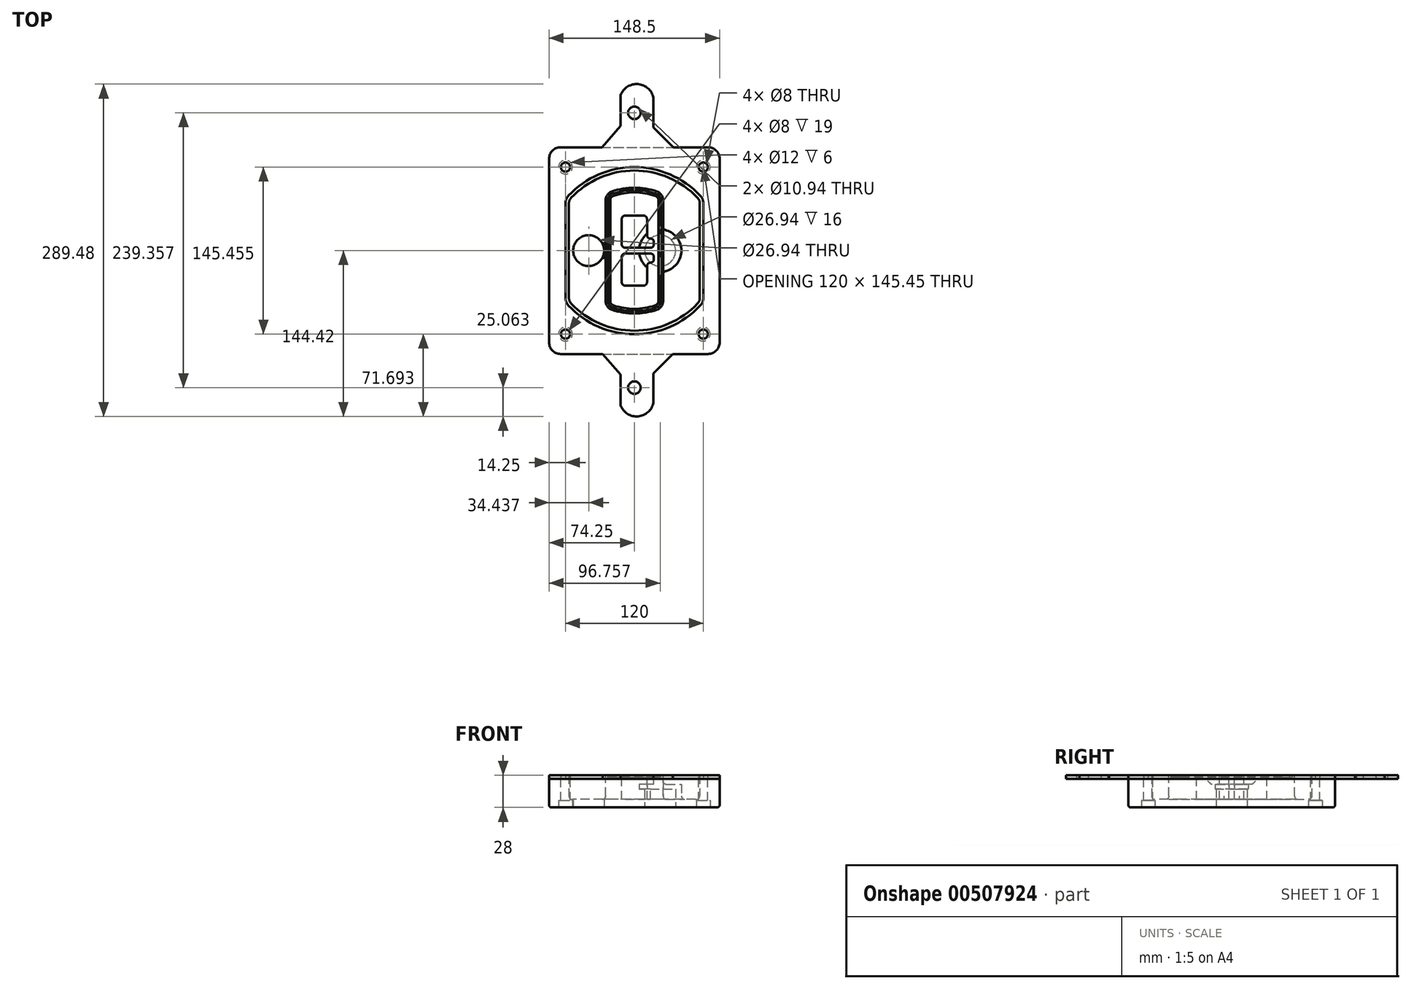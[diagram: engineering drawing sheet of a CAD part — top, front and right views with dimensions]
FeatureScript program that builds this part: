
annotation { "Feature Type Name" : "Feature", "Feature Type Description" : "" }
export const myFeature = defineFeature(function(context is Context, id is Id, definition is map)
    precondition{}
    {
        {
            var Q0;
            Q0=qCreatedBy(makeId("Top.planeOp"),FACE);
            var sketch = newSketch(context, id + "F0", { "sketchPlane" : qUnion([Q0])});
            skPoint(sketch, "E0.rect.middle", {"position": v(0, 0) * mm});
            skLineSegment(sketch, "E1.bottom", {"start": v(-64.25, -90) * mm, "end": v(64.25, -90) * mm});
            skLineSegment(sketch, "E1.top", {"start": v(-64.25, 90) * mm, "end": v(64.25, 90) * mm});
            skLineSegment(sketch, "E1.left", {"start": v(-74.25, -80) * mm, "end": v(-74.25, 80) * mm});
            skLineSegment(sketch, "E1.right", {"start": v(74.25, -80) * mm, "end": v(74.25, 80) * mm});
            skLineSegment(sketch, "E2", {"start": v(-74.25, 90) * mm, "end": v(74.25, -90) * mm, "construction": true});
            skLineSegment(sketch, "E3", {"start": v(74.25, 90) * mm, "end": v(-74.25, -90) * mm, "construction": true});
            skCircle(sketch, "E4", {"center": v(-60, 72.73) * mm, "radius": 4 * mm});
            skCircle(sketch, "E5", {"center": v(60, 72.73) * mm, "radius": 4 * mm});
            skCircle(sketch, "E6", {"center": v(60, -72.73) * mm, "radius": 4 * mm});
            skCircle(sketch, "E7", {"center": v(-60, -72.73) * mm, "radius": 4 * mm});
            skLineSegment(sketch, "E8", {"start": v(-60, 72.73) * mm, "end": v(60, 72.73) * mm, "construction": true});
            skLineSegment(sketch, "E9", {"start": v(60, 72.73) * mm, "end": v(60, -72.73) * mm, "construction": true});
            skLineSegment(sketch, "E10", {"start": v(60, -72.73) * mm, "end": v(-60, -72.73) * mm, "construction": true});
            skLineSegment(sketch, "E11", {"start": v(-60, -72.73) * mm, "end": v(-60, 72.73) * mm, "construction": true});
            skLineSegment(sketch, "E12", {"start": v(-60, 41.18) * mm, "end": v(-60, -41.18) * mm});
            skLineSegment(sketch, "E13", {"start": v(60, 41.18) * mm, "end": v(60, -41.18) * mm});
            skArc(sketch, "E14", {"start": v(57.27, 48.05) * mm, "mid": v(0, 72.73) * mm, "end": v(-57.27, 48.05) * mm});
            skArc(sketch, "E15", {"start": v(-57.27, -48.05) * mm, "mid": v(0, -72.73) * mm, "end": v(57.27, -48.05) * mm});
            skLineSegment(sketch, "E16", {"start": v(-60, 0) * mm, "end": v(60, 0) * mm, "construction": true});
            skPoint(sketch, "E17.visualSharp", {"position": v(-60, -45) * mm});
            skArc(sketch, "E17.filletArc", {"start": v(-60, -41.18) * mm, "mid": v(-59.3, -44.87) * mm, "end": v(-57.27, -48.05) * mm});
            skPoint(sketch, "E18.visualSharp", {"position": v(-60, 45) * mm});
            skArc(sketch, "E18.filletArc", {"start": v(-57.27, 48.05) * mm, "mid": v(-59.3, 44.87) * mm, "end": v(-60, 41.18) * mm});
            skPoint(sketch, "E19.visualSharp", {"position": v(60, 45) * mm});
            skArc(sketch, "E19.filletArc", {"start": v(60, 41.18) * mm, "mid": v(59.3, 44.87) * mm, "end": v(57.27, 48.05) * mm});
            skPoint(sketch, "E20.visualSharp", {"position": v(60, -45) * mm});
            skArc(sketch, "E20.filletArc", {"start": v(57.27, -48.05) * mm, "mid": v(59.3, -44.87) * mm, "end": v(60, -41.18) * mm});
            skPoint(sketch, "E21.visualSharp", {"position": v(-74.25, 90) * mm});
            skArc(sketch, "E21.filletArc", {"start": v(-64.25, 90) * mm, "mid": v(-71.32, 87.07) * mm, "end": v(-74.25, 80) * mm});
            skPoint(sketch, "E22.visualSharp", {"position": v(74.25, 90) * mm});
            skArc(sketch, "E22.filletArc", {"start": v(74.25, 80) * mm, "mid": v(71.32, 87.07) * mm, "end": v(64.25, 90) * mm});
            skPoint(sketch, "E23.visualSharp", {"position": v(74.25, -90) * mm});
            skArc(sketch, "E23.filletArc", {"start": v(64.25, -90) * mm, "mid": v(71.32, -87.07) * mm, "end": v(74.25, -80) * mm});
            skPoint(sketch, "E24.visualSharp", {"position": v(-74.25, -90) * mm});
            skArc(sketch, "E24.filletArc", {"start": v(-74.25, -80) * mm, "mid": v(-71.32, -87.07) * mm, "end": v(-64.25, -90) * mm});
            skArc(sketch, "E25.0", {"start": v(57, 41.18) * mm, "mid": v(56.5, 43.76) * mm, "end": v(55.09, 45.99) * mm});
            skLineSegment(sketch, "E25.1", {"start": v(57, 41.18) * mm, "end": v(57, -41.18) * mm});
            skArc(sketch, "E25.2", {"start": v(55.09, -45.99) * mm, "mid": v(56.5, -43.76) * mm, "end": v(57, -41.18) * mm});
            skArc(sketch, "E25.3", {"start": v(-55.09, -45.99) * mm, "mid": v(0, -69.73) * mm, "end": v(55.09, -45.99) * mm});
            skArc(sketch, "E25.4", {"start": v(-57, -41.18) * mm, "mid": v(-56.5, -43.76) * mm, "end": v(-55.09, -45.99) * mm});
            skArc(sketch, "E25.5", {"start": v(55.09, 45.99) * mm, "mid": v(0, 69.73) * mm, "end": v(-55.09, 45.99) * mm});
            skLineSegment(sketch, "E25.6", {"start": v(-57, 41.18) * mm, "end": v(-57, -41.18) * mm});
            skArc(sketch, "E25.7", {"start": v(-55.09, 45.99) * mm, "mid": v(-56.5, 43.76) * mm, "end": v(-57, 41.18) * mm});
            skArc(sketch, "E26.0", {"start": v(-60.18, 50.8) * mm, "mid": v(-63, 46.35) * mm, "end": v(-64, 41.18) * mm});
            skArc(sketch, "E26.1", {"start": v(60.18, 50.8) * mm, "mid": v(0, 76.73) * mm, "end": v(-60.18, 50.8) * mm});
            skArc(sketch, "E26.2", {"start": v(64, 41.18) * mm, "mid": v(63, 46.35) * mm, "end": v(60.18, 50.8) * mm});
            skLineSegment(sketch, "E26.3", {"start": v(64, 41.18) * mm, "end": v(64, -41.18) * mm});
            skArc(sketch, "E26.4", {"start": v(60.18, -50.8) * mm, "mid": v(63, -46.35) * mm, "end": v(64, -41.18) * mm});
            skLineSegment(sketch, "E26.5", {"start": v(-64, 41.18) * mm, "end": v(-64, -41.18) * mm});
            skArc(sketch, "E26.6", {"start": v(-60.18, -50.8) * mm, "mid": v(0, -76.73) * mm, "end": v(60.18, -50.8) * mm});
            skArc(sketch, "E26.7", {"start": v(-64, -41.18) * mm, "mid": v(-63, -46.35) * mm, "end": v(-60.18, -50.8) * mm});
            skSolve(sketch);
        }
        {
            var Q0;
            Q0=makeQuery(id+"F0.imprint","IMPRINT",FACE,{"disambiguationData":[TD([[makeQuery(id+"F0.imprint","IMPRINT",EDGE,{"derivedFrom":sQuery(id+"F0.wireOp",EDGE,"E1.bottom")}),1.0]])]});
            var Q1;
            Q1=makeQuery(id+"F0.imprint","IMPRINT",FACE,{"disambiguationData":[TD([[makeQuery(id+"F0.imprint","IMPRINT",EDGE,{"derivedFrom":sQuery(id+"F0.wireOp",EDGE,"E12")}),1.0]])]});
            var Q2;
            Q2=makeQuery(id+"F0.imprint","IMPRINT",FACE,{"disambiguationData":[TD([[makeQuery(id+"F0.imprint","IMPRINT",EDGE,{"derivedFrom":sQuery(id+"F0.wireOp",EDGE,"E25.0")}),1.0]])]});
            var Q3;
            Q3=makeQuery(id+"F0.imprint","IMPRINT",FACE,{"disambiguationData":[TD([[makeQuery(id+"F0.imprint","IMPRINT",EDGE,{"derivedFrom":sQuery(id+"F0.wireOp",EDGE,"E12")}),-1.0]])]});
            extrude(context, id + "F1", {"entities" : qUnion([Q0, Q1, Q2, Q3]), "oppositeDirection" : true, "depth" : 25 * mm});
        }
        {
            var Q0;
            Q0=makeQuery(id+"F0.imprint","IMPRINT",FACE,{"disambiguationData":[TD([[makeQuery(id+"F0.imprint","IMPRINT",EDGE,{"derivedFrom":sQuery(id+"F0.wireOp",EDGE,"E12")}),1.0]])]});
            extrude(context, id + "F2", {"entities" : qUnion([Q0]), "operationType" : NewBodyOperationType.ADD, "depth" : 3 * mm});
        }
        {
            var Q0;
            Q0=makeQuery(id+"F0.imprint","IMPRINT",FACE,{"disambiguationData":[TD([[makeQuery(id+"F0.imprint","IMPRINT",EDGE,{"derivedFrom":sQuery(id+"F0.wireOp",EDGE,"E25.0")}),1.0]])]});
            extrude(context, id + "F3", {"entities" : qUnion([Q0]), "operationType" : NewBodyOperationType.REMOVE, "oppositeDirection" : true, "depth" : 18 * mm});
        }
        {
            var Q0;
            Q0=makeQuery(id+"F2.opExtrude","CAP_FACE",FACE,{"disambiguationData":[OSD([sQuery(id+"F0.wireOp",EDGE,"E12"),sQuery(id+"F0.wireOp",EDGE,"E13"),sQuery(id+"F0.wireOp",EDGE,"E14"),sQuery(id+"F0.wireOp",EDGE,"E15"),sQuery(id+"F0.wireOp",EDGE,"E17.filletArc"),sQuery(id+"F0.wireOp",EDGE,"E18.filletArc"),sQuery(id+"F0.wireOp",EDGE,"E19.filletArc"),sQuery(id+"F0.wireOp",EDGE,"E20.filletArc"),sQuery(id+"F0.wireOp",EDGE,"E25.0"),sQuery(id+"F0.wireOp",EDGE,"E25.1"),sQuery(id+"F0.wireOp",EDGE,"E25.2"),sQuery(id+"F0.wireOp",EDGE,"E25.3"),sQuery(id+"F0.wireOp",EDGE,"E25.4"),sQuery(id+"F0.wireOp",EDGE,"E25.5"),sQuery(id+"F0.wireOp",EDGE,"E25.6"),sQuery(id+"F0.wireOp",EDGE,"E25.7")])],"isStart":false});
            var sketch = newSketch(context, id + "F4", { "sketchPlane" : qUnion([Q0])});
            skArc(sketch, "E27.0", {"start": v(-19.58, -51.49) * mm, "mid": v(0, -54.73) * mm, "end": v(19.58, -51.49) * mm});
            skArc(sketch, "E28.0", {"start": v(19.58, 51.49) * mm, "mid": v(0, 54.73) * mm, "end": v(-19.58, 51.49) * mm});
            skLineSegment(sketch, "E29", {"start": v(-25, 43.91) * mm, "end": v(-25, -43.91) * mm});
            skLineSegment(sketch, "E30", {"start": v(25, 43.91) * mm, "end": v(25, -43.91) * mm});
            skLineSegment(sketch, "E31", {"start": v(-25, 49.35) * mm, "end": v(25, 49.35) * mm, "construction": true});
            skLineSegment(sketch, "E32", {"start": v(-25, -49.35) * mm, "end": v(25, -49.35) * mm, "construction": true});
            skPoint(sketch, "E33.visualSharp", {"position": v(-25, 49.35) * mm});
            skArc(sketch, "E33.filletArc", {"start": v(-19.58, 51.49) * mm, "mid": v(-23.5, 48.57) * mm, "end": v(-25, 43.91) * mm});
            skPoint(sketch, "E34.visualSharp", {"position": v(25, 49.35) * mm});
            skArc(sketch, "E34.filletArc", {"start": v(25, 43.91) * mm, "mid": v(23.5, 48.57) * mm, "end": v(19.58, 51.49) * mm});
            skPoint(sketch, "E35.visualSharp", {"position": v(25, -49.35) * mm});
            skArc(sketch, "E35.filletArc", {"start": v(19.58, -51.49) * mm, "mid": v(23.5, -48.57) * mm, "end": v(25, -43.91) * mm});
            skPoint(sketch, "E36.visualSharp", {"position": v(-25, -49.35) * mm});
            skArc(sketch, "E36.filletArc", {"start": v(-25, -43.91) * mm, "mid": v(-23.5, -48.57) * mm, "end": v(-19.58, -51.49) * mm});
            skArc(sketch, "E37.0", {"start": v(55.09, 45.99) * mm, "mid": v(0, 69.73) * mm, "end": v(-55.09, 45.99) * mm});
            skArc(sketch, "E37.1", {"start": v(-55.09, 45.99) * mm, "mid": v(-56.5, 43.76) * mm, "end": v(-57, 41.18) * mm});
            skLineSegment(sketch, "E37.2", {"start": v(-57, 41.18) * mm, "end": v(-57, -41.18) * mm});
            skArc(sketch, "E37.3", {"start": v(-57, -41.18) * mm, "mid": v(-56.5, -43.76) * mm, "end": v(-55.09, -45.99) * mm});
            skArc(sketch, "E37.4", {"start": v(-55.09, -45.99) * mm, "mid": v(0, -69.73) * mm, "end": v(55.09, -45.99) * mm});
            skArc(sketch, "E37.5", {"start": v(55.09, -45.99) * mm, "mid": v(56.5, -43.76) * mm, "end": v(57, -41.18) * mm});
            skLineSegment(sketch, "E37.6", {"start": v(57, 41.18) * mm, "end": v(57, -41.18) * mm});
            skArc(sketch, "E37.7", {"start": v(57, 41.18) * mm, "mid": v(56.5, 43.76) * mm, "end": v(55.09, 45.99) * mm});
            skLineSegment(sketch, "E38.0", {"start": v(23, 43.91) * mm, "end": v(23, -43.91) * mm});
            skArc(sketch, "E38.1", {"start": v(18.93, -49.6) * mm, "mid": v(21.88, -47.4) * mm, "end": v(23, -43.91) * mm});
            skArc(sketch, "E38.2", {"start": v(-18.93, -49.6) * mm, "mid": v(0, -52.73) * mm, "end": v(18.93, -49.6) * mm});
            skArc(sketch, "E38.3", {"start": v(-23, -43.91) * mm, "mid": v(-21.88, -47.4) * mm, "end": v(-18.93, -49.6) * mm});
            skLineSegment(sketch, "E38.4", {"start": v(-23, 43.91) * mm, "end": v(-23, -43.91) * mm});
            skArc(sketch, "E38.5", {"start": v(23, 43.91) * mm, "mid": v(21.88, 47.4) * mm, "end": v(18.93, 49.6) * mm});
            skArc(sketch, "E38.6", {"start": v(-18.93, 49.6) * mm, "mid": v(-21.88, 47.4) * mm, "end": v(-23, 43.91) * mm});
            skArc(sketch, "E38.7", {"start": v(18.93, 49.6) * mm, "mid": v(0, 52.73) * mm, "end": v(-18.93, 49.6) * mm});
            skArc(sketch, "E39.0", {"start": v(21, 43.91) * mm, "mid": v(20.25, 46.24) * mm, "end": v(18.29, 47.7) * mm});
            skLineSegment(sketch, "E39.1", {"start": v(21, 43.91) * mm, "end": v(21, -43.91) * mm});
            skArc(sketch, "E39.2", {"start": v(18.29, -47.7) * mm, "mid": v(20.25, -46.24) * mm, "end": v(21, -43.91) * mm});
            skArc(sketch, "E39.3", {"start": v(-18.29, -47.7) * mm, "mid": v(0, -50.73) * mm, "end": v(18.29, -47.7) * mm});
            skArc(sketch, "E39.4", {"start": v(-21, -43.91) * mm, "mid": v(-20.25, -46.24) * mm, "end": v(-18.29, -47.7) * mm});
            skArc(sketch, "E39.5", {"start": v(18.29, 47.7) * mm, "mid": v(0, 50.73) * mm, "end": v(-18.29, 47.7) * mm});
            skLineSegment(sketch, "E39.6", {"start": v(-21, 43.91) * mm, "end": v(-21, -43.91) * mm});
            skArc(sketch, "E39.7", {"start": v(-18.29, 47.7) * mm, "mid": v(-20.25, 46.24) * mm, "end": v(-21, 43.91) * mm});
            skLineSegment(sketch, "E40", {"start": v(-25, 0) * mm, "end": v(25, 0) * mm, "construction": true});
            skLineSegment(sketch, "E41", {"start": v(-11, 5.5) * mm, "end": v(-11, 27.5) * mm});
            skLineSegment(sketch, "E42", {"start": v(-8, 30.5) * mm, "end": v(8, 30.5) * mm});
            skLineSegment(sketch, "E43", {"start": v(11, 27.5) * mm, "end": v(11, 13.5) * mm});
            skLineSegment(sketch, "E44", {"start": v(14, 10.5) * mm, "end": v(14, 10.5) * mm});
            skLineSegment(sketch, "E45", {"start": v(17, 7.5) * mm, "end": v(17, 5.5) * mm});
            skLineSegment(sketch, "E46", {"start": v(14, 2.5) * mm, "end": v(-8, 2.5) * mm});
            skPoint(sketch, "E47.visualSharp", {"position": v(-11, 30.5) * mm});
            skArc(sketch, "E47.filletArc", {"start": v(-8, 30.5) * mm, "mid": v(-10.12, 29.62) * mm, "end": v(-11, 27.5) * mm});
            skPoint(sketch, "E48.visualSharp", {"position": v(11, 30.5) * mm});
            skArc(sketch, "E48.filletArc", {"start": v(11, 27.5) * mm, "mid": v(10.12, 29.62) * mm, "end": v(8, 30.5) * mm});
            skPoint(sketch, "E49.visualSharp", {"position": v(11, 10.5) * mm});
            skArc(sketch, "E49.filletArc", {"start": v(11, 13.5) * mm, "mid": v(11.88, 11.38) * mm, "end": v(14, 10.5) * mm});
            skPoint(sketch, "E50.visualSharp", {"position": v(17, 10.5) * mm});
            skArc(sketch, "E50.filletArc", {"start": v(17, 7.5) * mm, "mid": v(16.12, 9.62) * mm, "end": v(14, 10.5) * mm});
            skPoint(sketch, "E51.visualSharp", {"position": v(17, 2.5) * mm});
            skArc(sketch, "E51.filletArc", {"start": v(14, 2.5) * mm, "mid": v(16.12, 3.38) * mm, "end": v(17, 5.5) * mm});
            skPoint(sketch, "E52.visualSharp", {"position": v(-11, 2.5) * mm});
            skArc(sketch, "E52.filletArc", {"start": v(-11, 5.5) * mm, "mid": v(-10.12, 3.38) * mm, "end": v(-8, 2.5) * mm});
            skLineSegment(sketch, "E53.0.MirrorCS", {"start": v(14, -2.5) * mm, "end": v(-8, -2.5) * mm});
            skArc(sketch, "E54.0.MirrorCS", {"start": v(-11, -5.5) * mm, "mid": v(-10.12, -3.38) * mm, "end": v(-8, -2.5) * mm});
            skLineSegment(sketch, "E55.0.MirrorCS", {"start": v(-11, -5.5) * mm, "end": v(-11, -27.5) * mm});
            skArc(sketch, "E56.0.MirrorCS", {"start": v(-8, -30.5) * mm, "mid": v(-10.12, -29.62) * mm, "end": v(-11, -27.5) * mm});
            skLineSegment(sketch, "E57.0.MirrorCS", {"start": v(-8, -30.5) * mm, "end": v(8, -30.5) * mm});
            skArc(sketch, "E58.0.MirrorCS", {"start": v(11, -27.5) * mm, "mid": v(10.12, -29.62) * mm, "end": v(8, -30.5) * mm});
            skLineSegment(sketch, "E59.0.MirrorCS", {"start": v(11, -27.5) * mm, "end": v(11, -13.5) * mm});
            skArc(sketch, "E60.0.MirrorCS", {"start": v(11, -13.5) * mm, "mid": v(11.88, -11.38) * mm, "end": v(14, -10.5) * mm});
            skArc(sketch, "E61.0.MirrorCS", {"start": v(17, -7.5) * mm, "mid": v(16.12, -9.62) * mm, "end": v(14, -10.5) * mm});
            skLineSegment(sketch, "E62.0.MirrorCS", {"start": v(17, -7.5) * mm, "end": v(17, -5.5) * mm});
            skArc(sketch, "E63.0.MirrorCS", {"start": v(14, -2.5) * mm, "mid": v(16.12, -3.38) * mm, "end": v(17, -5.5) * mm});
            skSolve(sketch);
        }
        {
            var Q0;
            Q0=makeQuery(id+"F4.imprint","IMPRINT",FACE,{"disambiguationData":[TD([[makeQuery(id+"F4.imprint","IMPRINT",EDGE,{"derivedFrom":sQuery(id+"F4.wireOp",EDGE,"E27.0")}),1.0]])]});
            var Q1;
            Q1=makeQuery(id+"F4.imprint","IMPRINT",FACE,{"disambiguationData":[TD([[makeQuery(id+"F4.imprint","IMPRINT",EDGE,{"derivedFrom":sQuery(id+"F4.wireOp",EDGE,"E38.0")}),-1.0]])]});
            var Q2;
            Q2=makeQuery(id+"F4.imprint","IMPRINT",FACE,{"disambiguationData":[TD([[makeQuery(id+"F4.imprint","IMPRINT",EDGE,{"derivedFrom":sQuery(id+"F4.wireOp",EDGE,"E39.0")}),1.0]])]});
            extrude(context, id + "F5", {"entities" : qUnion([Q0, Q1, Q2]), "operationType" : NewBodyOperationType.ADD, "endBound" : BoundingType.UP_TO_NEXT, "oppositeDirection" : true, "depth" : 25 * mm});
        }
        {
            var Q0;
            Q0=makeQuery(id+"F4.imprint","IMPRINT",FACE,{"disambiguationData":[TD([[makeQuery(id+"F4.imprint","IMPRINT",EDGE,{"derivedFrom":sQuery(id+"F4.wireOp",EDGE,"E38.0")}),-1.0]])]});
            extrude(context, id + "F6", {"entities" : qUnion([Q0]), "operationType" : NewBodyOperationType.REMOVE, "oppositeDirection" : true, "depth" : 2 * mm});
        }
        {
            var Q0;
            Q0=makeQuery(id+"F1.opExtrude","CAP_FACE",FACE,{"disambiguationData":[OSD([sQuery(id+"F0.wireOp",EDGE,"E1.bottom"),sQuery(id+"F0.wireOp",EDGE,"E1.top"),sQuery(id+"F0.wireOp",EDGE,"E1.left"),sQuery(id+"F0.wireOp",EDGE,"E1.right"),sQuery(id+"F0.wireOp",EDGE,"E4"),sQuery(id+"F0.wireOp",EDGE,"E5"),sQuery(id+"F0.wireOp",EDGE,"E6"),sQuery(id+"F0.wireOp",EDGE,"E7"),sQuery(id+"F0.wireOp",EDGE,"E21.filletArc"),sQuery(id+"F0.wireOp",EDGE,"E22.filletArc"),sQuery(id+"F0.wireOp",EDGE,"E23.filletArc"),sQuery(id+"F0.wireOp",EDGE,"E24.filletArc")])],"isStart":false});
            var sketch = newSketch(context, id + "F7", { "sketchPlane" : qUnion([Q0])});
            skCircle(sketch, "E64", {"center": v(22.5, 0) * mm, "radius": 13.47 * mm});
            skCircle(sketch, "E65", {"center": v(-39.81, 0) * mm, "radius": 13.47 * mm});
            skLineSegment(sketch, "E66", {"start": v(74.25, 0) * mm, "end": v(-74.25, 0) * mm});
            skCircle(sketch, "E67", {"center": v(22.5, 0) * mm, "radius": 18.47 * mm});
            skCircle(sketch, "E68", {"center": v(60, -72.73) * mm, "radius": 6 * mm});
            skCircle(sketch, "E69", {"center": v(-60, -72.73) * mm, "radius": 6 * mm});
            skCircle(sketch, "E70", {"center": v(-60, 72.73) * mm, "radius": 6 * mm});
            skCircle(sketch, "E71", {"center": v(60, 72.73) * mm, "radius": 6 * mm});
            skSolve(sketch);
        }
        {
            var Q0;
            {var subQ1=sQuery(id+"F7.wireOp",EDGE,"E66");var subQ4=sQuery(id+"F7.wireOp",EDGE,"E64");var subQ6=makeQuery(id+"F7.imprint","INTERSECT",VERTEX,{"disambiguationData":[OD(0.0)],"derivedFrom":[subQ4,subQ1]});Q0=makeQuery(id+"F7.imprint","IMPRINT",FACE,{"disambiguationData":[TD([[makeQuery(id+"F7.imprint","IMPRINT",EDGE,{"disambiguationData":[TD([[subQ6,-1.0]])],"derivedFrom":subQ4}),-1.0]])]});}
            var Q1;
            {var subQ0=sQuery(id+"F7.wireOp",EDGE,"E66");var subQ1=sQuery(id+"F7.wireOp",EDGE,"E64");var subQ3=makeQuery(id+"F7.imprint","INTERSECT",VERTEX,{"disambiguationData":[OD(0.0)],"derivedFrom":[subQ1,subQ0]});Q1=makeQuery(id+"F7.imprint","IMPRINT",FACE,{"disambiguationData":[TD([[makeQuery(id+"F7.imprint","IMPRINT",EDGE,{"disambiguationData":[TD([[subQ3,-1.0]])],"derivedFrom":subQ1}),1.0]])]});}
            var Q2;
            {var subQ0=sQuery(id+"F7.wireOp",EDGE,"E66");var subQ1=sQuery(id+"F7.wireOp",EDGE,"E64");var subQ3=makeQuery(id+"F7.imprint","INTERSECT",VERTEX,{"disambiguationData":[OD(0.0)],"derivedFrom":[subQ1,subQ0]});Q2=makeQuery(id+"F7.imprint","IMPRINT",FACE,{"disambiguationData":[TD([[makeQuery(id+"F7.imprint","IMPRINT",EDGE,{"disambiguationData":[TD([[subQ3,1.0]])],"derivedFrom":subQ1}),1.0]])]});}
            var Q3;
            {var subQ1=sQuery(id+"F7.wireOp",EDGE,"E66");var subQ4=sQuery(id+"F7.wireOp",EDGE,"E64");var subQ6=makeQuery(id+"F7.imprint","INTERSECT",VERTEX,{"disambiguationData":[OD(0.0)],"derivedFrom":[subQ4,subQ1]});Q3=makeQuery(id+"F7.imprint","IMPRINT",FACE,{"disambiguationData":[TD([[makeQuery(id+"F7.imprint","IMPRINT",EDGE,{"disambiguationData":[TD([[subQ6,1.0]])],"derivedFrom":subQ4}),-1.0]])]});}
            extrude(context, id + "F8", {"entities" : qUnion([Q0, Q1, Q2, Q3]), "operationType" : NewBodyOperationType.ADD, "oppositeDirection" : true, "depth" : 20 * mm});
        }
        {
            var Q0;
            {var subQ0=sQuery(id+"F7.wireOp",EDGE,"E66");var subQ1=sQuery(id+"F7.wireOp",EDGE,"E64");var subQ3=makeQuery(id+"F7.imprint","INTERSECT",VERTEX,{"disambiguationData":[OD(0.0)],"derivedFrom":[subQ1,subQ0]});Q0=makeQuery(id+"F7.imprint","IMPRINT",FACE,{"disambiguationData":[TD([[makeQuery(id+"F7.imprint","IMPRINT",EDGE,{"disambiguationData":[TD([[subQ3,-1.0]])],"derivedFrom":subQ1}),1.0]])]});}
            var Q1;
            {var subQ0=sQuery(id+"F7.wireOp",EDGE,"E66");var subQ1=sQuery(id+"F7.wireOp",EDGE,"E64");var subQ3=makeQuery(id+"F7.imprint","INTERSECT",VERTEX,{"disambiguationData":[OD(0.0)],"derivedFrom":[subQ1,subQ0]});Q1=makeQuery(id+"F7.imprint","IMPRINT",FACE,{"disambiguationData":[TD([[makeQuery(id+"F7.imprint","IMPRINT",EDGE,{"disambiguationData":[TD([[subQ3,1.0]])],"derivedFrom":subQ1}),1.0]])]});}
            extrude(context, id + "F9", {"entities" : qUnion([Q0, Q1]), "operationType" : NewBodyOperationType.REMOVE, "oppositeDirection" : true, "depth" : 16 * mm});
        }
        {
            var Q0;
            {var subQ0=sQuery(id+"F7.wireOp",EDGE,"E66");var subQ1=sQuery(id+"F7.wireOp",EDGE,"E65");var subQ3=makeQuery(id+"F7.imprint","INTERSECT",VERTEX,{"disambiguationData":[OD(0.0)],"derivedFrom":[subQ1,subQ0]});Q0=makeQuery(id+"F7.imprint","IMPRINT",FACE,{"disambiguationData":[TD([[makeQuery(id+"F7.imprint","IMPRINT",EDGE,{"disambiguationData":[TD([[subQ3,-1.0]])],"derivedFrom":subQ1}),1.0]])]});}
            var Q1;
            {var subQ0=sQuery(id+"F7.wireOp",EDGE,"E66");var subQ1=sQuery(id+"F7.wireOp",EDGE,"E65");var subQ3=makeQuery(id+"F7.imprint","INTERSECT",VERTEX,{"disambiguationData":[OD(0.0)],"derivedFrom":[subQ1,subQ0]});Q1=makeQuery(id+"F7.imprint","IMPRINT",FACE,{"disambiguationData":[TD([[makeQuery(id+"F7.imprint","IMPRINT",EDGE,{"disambiguationData":[TD([[subQ3,1.0]])],"derivedFrom":subQ1}),1.0]])]});}
            extrude(context, id + "F10", {"entities" : qUnion([Q0, Q1]), "operationType" : NewBodyOperationType.REMOVE, "oppositeDirection" : true, "depth" : 25 * mm});
        }
        {
            var Q0;
            Q0=makeQuery(id+"F7.imprint","IMPRINT",FACE,{"disambiguationData":[TD([[makeQuery(id+"F7.imprint","IMPRINT",EDGE,{"derivedFrom":sQuery(id+"F7.wireOp",EDGE,"E68")}),1.0]])]});
            var Q1;
            Q1=makeQuery(id+"F7.imprint","IMPRINT",FACE,{"disambiguationData":[TD([[makeQuery(id+"F7.imprint","IMPRINT",EDGE,{"derivedFrom":makeQuery(id+"F1.opExtrude","CAP_EDGE",EDGE,{"disambiguationData":[OSD([sQuery(id+"F0.wireOp",EDGE,"E5")])],"isStart":false})}),-1.0]])]});
            var Q2;
            Q2=makeQuery(id+"F7.imprint","IMPRINT",FACE,{"disambiguationData":[TD([[makeQuery(id+"F7.imprint","IMPRINT",EDGE,{"derivedFrom":sQuery(id+"F7.wireOp",EDGE,"E69")}),1.0]])]});
            var Q3;
            Q3=makeQuery(id+"F7.imprint","IMPRINT",FACE,{"disambiguationData":[TD([[makeQuery(id+"F7.imprint","IMPRINT",EDGE,{"derivedFrom":makeQuery(id+"F1.opExtrude","CAP_EDGE",EDGE,{"disambiguationData":[OSD([sQuery(id+"F0.wireOp",EDGE,"E4")])],"isStart":false})}),-1.0]])]});
            var Q4;
            Q4=makeQuery(id+"F7.imprint","IMPRINT",FACE,{"disambiguationData":[TD([[makeQuery(id+"F7.imprint","IMPRINT",EDGE,{"derivedFrom":sQuery(id+"F7.wireOp",EDGE,"E70")}),1.0]])]});
            var Q5;
            Q5=makeQuery(id+"F7.imprint","IMPRINT",FACE,{"disambiguationData":[TD([[makeQuery(id+"F7.imprint","IMPRINT",EDGE,{"derivedFrom":makeQuery(id+"F1.opExtrude","CAP_EDGE",EDGE,{"disambiguationData":[OSD([sQuery(id+"F0.wireOp",EDGE,"E7")])],"isStart":false})}),-1.0]])]});
            var Q6;
            Q6=makeQuery(id+"F7.imprint","IMPRINT",FACE,{"disambiguationData":[TD([[makeQuery(id+"F7.imprint","IMPRINT",EDGE,{"derivedFrom":sQuery(id+"F7.wireOp",EDGE,"E71")}),1.0]])]});
            var Q7;
            Q7=makeQuery(id+"F7.imprint","IMPRINT",FACE,{"disambiguationData":[TD([[makeQuery(id+"F7.imprint","IMPRINT",EDGE,{"derivedFrom":makeQuery(id+"F1.opExtrude","CAP_EDGE",EDGE,{"disambiguationData":[OSD([sQuery(id+"F0.wireOp",EDGE,"E6")])],"isStart":false})}),-1.0]])]});
            extrude(context, id + "F11", {"entities" : qUnion([Q0, Q1, Q2, Q3, Q4, Q5, Q6, Q7]), "operationType" : NewBodyOperationType.REMOVE, "oppositeDirection" : true, "depth" : 6 * mm});
        }
        {
            var Q0;
            Q0=makeQuery(id+"F9.boolean.opBoolean","COPY",FACE,{"derivedFrom":makeQuery(id+"F9.opExtrude","CAP_FACE",FACE,{"disambiguationData":[OSD([sQuery(id+"F7.wireOp",EDGE,"E64")])],"isStart":false})});
            var sketch = newSketch(context, id + "F12", { "sketchPlane" : qUnion([Q0])});
            skArc(sketch, "E72.0", {"start": v(11, 14.45) * mm, "mid": v(6.45, 9.13) * mm, "end": v(4.2, 2.5) * mm});
            skArc(sketch, "E72.1", {"start": v(4.2, -2.5) * mm, "mid": v(6.45, -9.13) * mm, "end": v(11, -14.45) * mm});
            skLineSegment(sketch, "E73", {"start": v(4.2, -2.5) * mm, "end": v(14, -2.5) * mm});
            skLineSegment(sketch, "E74.0", {"start": v(14, 2.5) * mm, "end": v(4.2, 2.5) * mm});
            skArc(sketch, "E74.1", {"start": v(14, 2.5) * mm, "mid": v(16.12, 3.38) * mm, "end": v(17, 5.5) * mm});
            skLineSegment(sketch, "E74.2", {"start": v(17, 7.5) * mm, "end": v(17, 5.5) * mm});
            skArc(sketch, "E74.3", {"start": v(17, 7.5) * mm, "mid": v(16.12, 9.62) * mm, "end": v(14, 10.5) * mm});
            skArc(sketch, "E74.4", {"start": v(11, 13.5) * mm, "mid": v(11.88, 11.38) * mm, "end": v(14, 10.5) * mm});
            skLineSegment(sketch, "E74.5", {"start": v(11, 14.45) * mm, "end": v(11, 13.5) * mm});
            skLineSegment(sketch, "E74.7", {"start": v(14, -2.5) * mm, "end": v(4.2, -2.5) * mm});
            skArc(sketch, "E74.8", {"start": v(14, -2.5) * mm, "mid": v(16.12, -3.38) * mm, "end": v(17, -5.5) * mm});
            skLineSegment(sketch, "E74.9", {"start": v(17, -7.5) * mm, "end": v(17, -5.5) * mm});
            skArc(sketch, "E74.10", {"start": v(17, -7.5) * mm, "mid": v(16.12, -9.62) * mm, "end": v(14, -10.5) * mm});
            skArc(sketch, "E74.11", {"start": v(11, -13.5) * mm, "mid": v(11.88, -11.38) * mm, "end": v(14, -10.5) * mm});
            skLineSegment(sketch, "E74.12", {"start": v(11, -14.45) * mm, "end": v(11, -13.5) * mm});
            skPoint(sketch, "E75.orphan", {"position": v(11, -27.5) * mm});
            skPoint(sketch, "E76.orphan", {"position": v(-8, -2.5) * mm});
            skPoint(sketch, "E77.orphan", {"position": v(-8, 2.5) * mm});
            skPoint(sketch, "E78.orphan", {"position": v(11, 27.5) * mm});
            skSolve(sketch);
        }
        {
            var Q0;
            {var subQ7=sQuery(id+"F12.wireOp",EDGE,"E72.0");var subQ14=sQuery(id+"F12.wireOp",EDGE,"E72.1");var subQ16=sQuery(id+"F12.wireOp",EDGE,"E74.1");var subQ18=sQuery(id+"F12.wireOp",EDGE,"E74.8");Q0=qUnion([makeQuery(id+"F12.imprint","IMPRINT",FACE,{"disambiguationData":[TD([[makeQuery(id+"F12.imprint","IMPRINT",EDGE,{"derivedFrom":subQ7}),1.0]])]}),makeQuery(id+"F12.imprint","IMPRINT",FACE,{"disambiguationData":[TD([[makeQuery(id+"F12.imprint","IMPRINT",EDGE,{"derivedFrom":subQ14}),1.0]])]}),makeQuery(id+"F12.imprint","IMPRINT",FACE,{"disambiguationData":[TD([[makeQuery(id+"F12.imprint","IMPRINT",EDGE,{"derivedFrom":subQ16}),1.0]])]}),makeQuery(id+"F12.imprint","IMPRINT",FACE,{"disambiguationData":[TD([[makeQuery(id+"F12.imprint","IMPRINT",EDGE,{"derivedFrom":subQ18}),-1.0]])]})]);}
            var Q1;
            Q1=makeQuery(id+"F5.boolean.opBoolean","SPLIT",FACE,{"disambiguationData":[TD([makeQuery(id+"F5.opExtrude","SWEPT_FACE",FACE,{"disambiguationData":[OSD([sQuery(id+"F4.wireOp",EDGE,"E41")])]})])],"derivedFrom":makeQuery(id+"F3.boolean.opBoolean","COPY",FACE,{"derivedFrom":makeQuery(id+"F3.opExtrude","CAP_FACE",FACE,{"disambiguationData":[OSD([sQuery(id+"F0.wireOp",EDGE,"E25.0"),sQuery(id+"F0.wireOp",EDGE,"E25.1"),sQuery(id+"F0.wireOp",EDGE,"E25.2"),sQuery(id+"F0.wireOp",EDGE,"E25.3"),sQuery(id+"F0.wireOp",EDGE,"E25.4"),sQuery(id+"F0.wireOp",EDGE,"E25.5"),sQuery(id+"F0.wireOp",EDGE,"E25.6"),sQuery(id+"F0.wireOp",EDGE,"E25.7")])],"isStart":false})})});
            extrude(context, id + "F13", {"entities" : qUnion([Q0]), "operationType" : NewBodyOperationType.REMOVE, "endBound" : BoundingType.UP_TO_SURFACE, "endBoundEntityFace" : qUnion([Q1]), "depth" : 25 * mm});
        }
        {
            var Q0;
            Q0=makeQuery(id+"F3.boolean.opBoolean","COPY",EDGE,{"derivedFrom":makeQuery(id+"F3.opExtrude","CAP_EDGE",EDGE,{"disambiguationData":[OSD([sQuery(id+"F0.wireOp",EDGE,"E25.6")])],"isStart":false})});
            var Q1;
            Q1=makeQuery(id+"F8.boolean.opBoolean","INTERSECT",EDGE,{"derivedFrom":[makeQuery(id+"F5.opExtrude","SWEPT_FACE",FACE,{"disambiguationData":[OSD([sQuery(id+"F4.wireOp",EDGE,"E30")])]}),makeQuery(id+"F8.opExtrude","CAP_FACE",FACE,{"disambiguationData":[OSD([sQuery(id+"F7.wireOp",EDGE,"E67")])],"isStart":false})]});
            var Q2;
            Q2=makeQuery(id+"F8.boolean.opBoolean","INTERSECT",EDGE,{"disambiguationData":[OD(1.0)],"derivedFrom":[makeQuery(id+"F5.opExtrude","SWEPT_FACE",FACE,{"disambiguationData":[OSD([sQuery(id+"F4.wireOp",EDGE,"E30")])]}),makeQuery(id+"F8.opExtrude","SWEPT_FACE",FACE,{"disambiguationData":[OSD([sQuery(id+"F7.wireOp",EDGE,"E67")])]})]});
            var Q3;
            {var subQ0=sQuery(id+"F4.wireOp",EDGE,"E30");Q3=makeQuery(id+"F8.boolean.opBoolean","SPLIT",EDGE,{"disambiguationData":[TD([makeQuery(id+"F5.opExtrude","SWEPT_FACE",FACE,{"disambiguationData":[OSD([sQuery(id+"F4.wireOp",EDGE,"E35.filletArc")])]})])],"derivedFrom":makeQuery(id+"F5.opExtrude","CAP_EDGE",EDGE,{"disambiguationData":[OSD([subQ0])],"isStart":false})});}
            var Q4;
            {var subQ0=sQuery(id+"F0.wireOp",EDGE,"E25.7");var subQ1=sQuery(id+"F0.wireOp",EDGE,"E25.1");var subQ2=sQuery(id+"F0.wireOp",EDGE,"E25.6");var subQ3=sQuery(id+"F0.wireOp",EDGE,"E25.5");var subQ4=sQuery(id+"F0.wireOp",EDGE,"E25.4");var subQ5=sQuery(id+"F0.wireOp",EDGE,"E25.0");var subQ6=sQuery(id+"F0.wireOp",EDGE,"E25.2");var subQ7=sQuery(id+"F0.wireOp",EDGE,"E25.3");Q4=makeQuery(id+"F8.boolean.opBoolean","INTERSECT",EDGE,{"derivedFrom":[makeQuery(id+"F5.boolean.opBoolean","SPLIT",FACE,{"disambiguationData":[TD([makeQuery(id+"F2.opExtrude","SWEPT_FACE",FACE,{"disambiguationData":[OSD([subQ5])]})])],"derivedFrom":makeQuery(id+"F3.boolean.opBoolean","COPY",FACE,{"derivedFrom":makeQuery(id+"F3.opExtrude","CAP_FACE",FACE,{"disambiguationData":[OSD([subQ5,subQ1,subQ6,subQ7,subQ4,subQ3,subQ2,subQ0])],"isStart":false})})}),makeQuery(id+"F8.opExtrude","SWEPT_FACE",FACE,{"disambiguationData":[OSD([sQuery(id+"F7.wireOp",EDGE,"E67")])]})]});}
            var Q5;
            Q5=makeQuery(id+"F8.boolean.opBoolean","INTERSECT",EDGE,{"disambiguationData":[OD(0.0)],"derivedFrom":[makeQuery(id+"F5.opExtrude","SWEPT_FACE",FACE,{"disambiguationData":[OSD([sQuery(id+"F4.wireOp",EDGE,"E30")])]}),makeQuery(id+"F8.opExtrude","SWEPT_FACE",FACE,{"disambiguationData":[OSD([sQuery(id+"F7.wireOp",EDGE,"E67")])]})]});
            fillet(context, id + "F14", {"entities" : qUnion([Q0, Q1, Q2, Q3, Q4, Q5]), "radius" : 3 * mm, "tangentPropagation" : true, "allowEdgeOverflow" : false});
        }
        {
            var Q0;
            Q0=makeQuery(id+"F1.opExtrude","CAP_EDGE",EDGE,{"disambiguationData":[OSD([sQuery(id+"F0.wireOp",EDGE,"E1.bottom")])],"isStart":false});
            fillet(context, id + "F15", {"entities" : qUnion([Q0]), "radius" : 2 * mm, "tangentPropagation" : true, "allowEdgeOverflow" : false});
        }
        {
            var Q0;
            {var subQ0=sQuery(id+"F0.wireOp",EDGE,"E21.filletArc");var subQ1=sQuery(id+"F0.wireOp",EDGE,"E7");var subQ2=sQuery(id+"F0.wireOp",EDGE,"E6");var subQ3=sQuery(id+"F0.wireOp",EDGE,"E5");var subQ4=sQuery(id+"F0.wireOp",EDGE,"E4");var subQ5=sQuery(id+"F0.wireOp",EDGE,"E22.filletArc");var subQ6=sQuery(id+"F0.wireOp",EDGE,"E1.bottom");var subQ7=sQuery(id+"F0.wireOp",EDGE,"E1.right");var subQ8=sQuery(id+"F0.wireOp",EDGE,"E1.top");var subQ9=sQuery(id+"F0.wireOp",EDGE,"E1.left");var subQ10=sQuery(id+"F0.wireOp",EDGE,"E23.filletArc");var subQ11=sQuery(id+"F0.wireOp",EDGE,"E24.filletArc");Q0=makeQuery(id+"F2.boolean.opBoolean","SPLIT",FACE,{"disambiguationData":[TD([makeQuery(id+"F1.opExtrude","SWEPT_FACE",FACE,{"disambiguationData":[OSD([subQ6])]})])],"derivedFrom":makeQuery(id+"F1.opExtrude","CAP_FACE",FACE,{"disambiguationData":[OSD([subQ6,subQ8,subQ9,subQ7,subQ4,subQ3,subQ2,subQ1,subQ0,subQ5,subQ10,subQ11])],"isStart":true})});}
            var sketch = newSketch(context, id + "F16", { "sketchPlane" : qUnion([Q0])});
            skSolve(sketch);
        }
        {
            var Q0;
            Q0=makeQuery(id+"F16.imprint","IMPRINT",FACE,{"disambiguationData":[TD([[makeQuery(id+"F16.imprint","IMPRINT",EDGE,{"derivedFrom":makeQuery(id+"F1.opExtrude","CAP_EDGE",EDGE,{"disambiguationData":[OSD([sQuery(id+"F0.wireOp",EDGE,"E1.bottom")])],"isStart":true})}),1.0]])]});
            var sketch = newSketch(context, id + "F17", { "sketchPlane" : qUnion([Q0])});
            skLineSegment(sketch, "E79.0", {"start": v(-64.25, 90) * mm, "end": v(64.25, 90) * mm});
            skArc(sketch, "E79.1", {"start": v(-64.25, 90) * mm, "mid": v(-71.32, 87.07) * mm, "end": v(-74.25, 80) * mm});
            skLineSegment(sketch, "E79.2", {"start": v(-74.25, -80) * mm, "end": v(-74.25, 80) * mm});
            skArc(sketch, "E79.3", {"start": v(-74.25, -80) * mm, "mid": v(-71.32, -87.07) * mm, "end": v(-64.25, -90) * mm});
            skLineSegment(sketch, "E79.4", {"start": v(-64.25, -90) * mm, "end": v(64.25, -90) * mm});
            skArc(sketch, "E79.5", {"start": v(64.25, -90) * mm, "mid": v(71.32, -87.07) * mm, "end": v(74.25, -80) * mm});
            skLineSegment(sketch, "E79.6", {"start": v(74.25, -80) * mm, "end": v(74.25, 80) * mm});
            skArc(sketch, "E79.7", {"start": v(74.25, 80) * mm, "mid": v(71.32, 87.07) * mm, "end": v(64.25, 90) * mm});
            skCircle(sketch, "E79.8", {"center": v(60, 72.73) * mm, "radius": 4 * mm});
            skCircle(sketch, "E79.9", {"center": v(-60, 72.73) * mm, "radius": 4 * mm});
            skCircle(sketch, "E79.10", {"center": v(-60, -72.73) * mm, "radius": 4 * mm});
            skCircle(sketch, "E79.11", {"center": v(60, -72.73) * mm, "radius": 4 * mm});
            skArc(sketch, "E79.12", {"start": v(57.27, -48.05) * mm, "mid": v(59.3, -44.87) * mm, "end": v(60, -41.18) * mm});
            skArc(sketch, "E79.13", {"start": v(-57.27, -48.05) * mm, "mid": v(0, -72.73) * mm, "end": v(57.27, -48.05) * mm});
            skLineSegment(sketch, "E79.14", {"start": v(-60, 41.18) * mm, "end": v(-60, -41.18) * mm});
            skArc(sketch, "E79.15", {"start": v(-60, -41.18) * mm, "mid": v(-59.3, -44.87) * mm, "end": v(-57.27, -48.05) * mm});
            skArc(sketch, "E79.16", {"start": v(57.27, 48.05) * mm, "mid": v(0, 72.73) * mm, "end": v(-57.27, 48.05) * mm});
            skArc(sketch, "E79.17", {"start": v(-57.27, 48.05) * mm, "mid": v(-59.3, 44.87) * mm, "end": v(-60, 41.18) * mm});
            skLineSegment(sketch, "E79.18", {"start": v(60, 41.18) * mm, "end": v(60, -41.18) * mm});
            skArc(sketch, "E79.19", {"start": v(60, 41.18) * mm, "mid": v(59.3, 44.87) * mm, "end": v(57.27, 48.05) * mm});
            skLineSegment(sketch, "E80", {"start": v(0, 90) * mm, "end": v(0, 120) * mm, "construction": true});
            skPoint(sketch, "E80.endSnap0", {"position": v(0, 90) * mm});
            skLineSegment(sketch, "E81", {"start": v(16.63, 107.49) * mm, "end": v(16.63, 133.24) * mm});
            skLineSegment(sketch, "E82", {"start": v(-11.96, 108.68) * mm, "end": v(-11.96, 135.64) * mm});
            skArc(sketch, "E83", {"start": v(16.63, 133.24) * mm, "mid": v(3.22, 145) * mm, "end": v(-11.96, 135.64) * mm});
            skLineSegment(sketch, "E84", {"start": v(16.63, 107.49) * mm, "end": v(34.11, 90) * mm});
            skLineSegment(sketch, "E85", {"start": v(-11.96, 108.68) * mm, "end": v(-28.16, 90) * mm});
            skLineSegment(sketch, "E86", {"start": v(-74.25, 0.32) * mm, "end": v(74.25, 0.32) * mm, "construction": true});
            skCircle(sketch, "E87", {"center": v(0, 120) * mm, "radius": 5.47 * mm});
            skLineSegment(sketch, "E88.MirrorCS", {"start": v(0, -89.36) * mm, "end": v(0, -119.36) * mm, "construction": true});
            skCircle(sketch, "E89.MirrorC", {"center": v(0, -119.36) * mm, "radius": 5.47 * mm});
            skLineSegment(sketch, "E90.MirrorCS", {"start": v(16.63, -106.84) * mm, "end": v(34.11, -89.36) * mm});
            skLineSegment(sketch, "E91.MirrorCS", {"start": v(16.63, -106.84) * mm, "end": v(16.63, -132.6) * mm});
            skArc(sketch, "E92.MirrorCS", {"start": v(16.63, -132.6) * mm, "mid": v(3.22, -144.36) * mm, "end": v(-11.96, -135) * mm});
            skLineSegment(sketch, "E93.MirrorCS", {"start": v(-11.96, -108.03) * mm, "end": v(-11.96, -135) * mm});
            skLineSegment(sketch, "E94.MirrorCS", {"start": v(-11.96, -108.03) * mm, "end": v(-28.16, -89.36) * mm});
            skSolve(sketch);
        }
        {
            var Q0;
            Q0 = qSketchRegion(id + "F17", true);
            var Q1;
            Q1=makeQuery(id+"F2.opExtrude","CAP_FACE",FACE,{"disambiguationData":[OSD([sQuery(id+"F0.wireOp",EDGE,"E12"),sQuery(id+"F0.wireOp",EDGE,"E13"),sQuery(id+"F0.wireOp",EDGE,"E14"),sQuery(id+"F0.wireOp",EDGE,"E15"),sQuery(id+"F0.wireOp",EDGE,"E17.filletArc"),sQuery(id+"F0.wireOp",EDGE,"E18.filletArc"),sQuery(id+"F0.wireOp",EDGE,"E19.filletArc"),sQuery(id+"F0.wireOp",EDGE,"E20.filletArc"),sQuery(id+"F0.wireOp",EDGE,"E25.0"),sQuery(id+"F0.wireOp",EDGE,"E25.1"),sQuery(id+"F0.wireOp",EDGE,"E25.2"),sQuery(id+"F0.wireOp",EDGE,"E25.3"),sQuery(id+"F0.wireOp",EDGE,"E25.4"),sQuery(id+"F0.wireOp",EDGE,"E25.5"),sQuery(id+"F0.wireOp",EDGE,"E25.6"),sQuery(id+"F0.wireOp",EDGE,"E25.7")])],"isStart":false});
            extrude(context, id + "F18", {"entities" : qUnion([Q0]), "endBound" : BoundingType.UP_TO_SURFACE, "endBoundEntityFace" : qUnion([Q1]), "depth" : 25 * mm});
        }
    });
